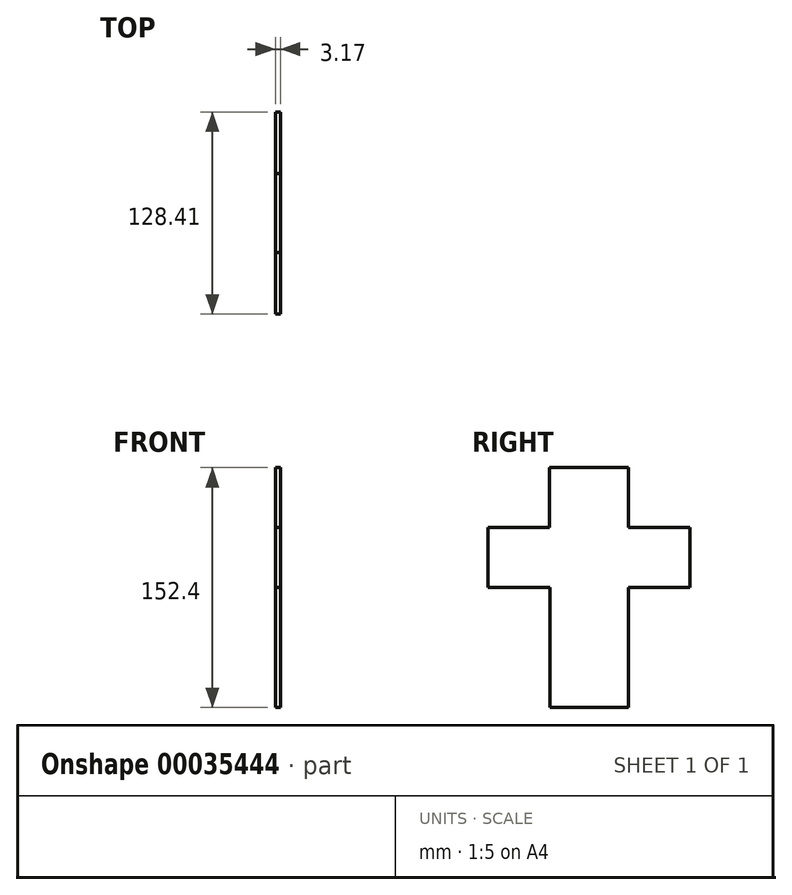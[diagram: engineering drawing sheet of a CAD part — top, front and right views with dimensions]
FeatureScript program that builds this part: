
annotation { "Feature Type Name" : "Feature", "Feature Type Description" : "" }
export const myFeature = defineFeature(function(context is Context, id is Id, definition is map)
    precondition{}
    {
        {
            var Q0;
            Q0=qCreatedBy(makeId("Right.planeOp"),FACE);
            var sketch = newSketch(context, id + "F0", { "sketchPlane" : qUnion([Q0])});
            skLineSegment(sketch, "E0.bottom", {"start": v(0, -2) * mm, "end": v(-49.92, -2) * mm});
            skLineSegment(sketch, "E0.top", {"start": v(0, -40.1) * mm, "end": v(-49.92, -40.1) * mm});
            skLineSegment(sketch, "E0.left", {"start": v(0, -2) * mm, "end": v(0, -40.1) * mm});
            skLineSegment(sketch, "E0.right", {"start": v(-49.92, -2) * mm, "end": v(-49.92, -40.1) * mm});
            skLineSegment(sketch, "E1.bottom", {"start": v(0, -2) * mm, "end": v(-50.15, -2) * mm});
            skLineSegment(sketch, "E1.top", {"start": v(0, 36.1) * mm, "end": v(-50.15, 36.1) * mm});
            skLineSegment(sketch, "E1.left", {"start": v(0, -2) * mm, "end": v(0, 36.1) * mm});
            skLineSegment(sketch, "E1.right", {"start": v(-50.15, -2) * mm, "end": v(-50.15, 36.1) * mm});
            skLineSegment(sketch, "E2.top", {"start": v(0, 74.2) * mm, "end": v(-50.15, 74.2) * mm});
            skLineSegment(sketch, "E2.left", {"start": v(0, 36.1) * mm, "end": v(0, 74.2) * mm});
            skLineSegment(sketch, "E2.right", {"start": v(-50.15, 36.1) * mm, "end": v(-50.15, 74.2) * mm});
            skLineSegment(sketch, "E3.top", {"start": v(0, -78.2) * mm, "end": v(-49.92, -78.2) * mm});
            skLineSegment(sketch, "E3.left", {"start": v(0, -40.1) * mm, "end": v(0, -78.2) * mm});
            skLineSegment(sketch, "E3.right", {"start": v(-49.92, -40.1) * mm, "end": v(-49.92, -78.2) * mm});
            skLineSegment(sketch, "E4.bottom", {"start": v(0, 36.1) * mm, "end": v(39.22, 36.1) * mm});
            skLineSegment(sketch, "E4.top", {"start": v(0, -2) * mm, "end": v(39.22, -2) * mm});
            skLineSegment(sketch, "E4.left", {"start": v(0, 36.1) * mm, "end": v(0, -2) * mm});
            skLineSegment(sketch, "E4.right", {"start": v(39.22, 36.1) * mm, "end": v(39.22, -2) * mm});
            skLineSegment(sketch, "E5.bottom", {"start": v(-50.15, 36.1) * mm, "end": v(-89.2, 36.1) * mm});
            skLineSegment(sketch, "E5.top", {"start": v(-50.15, -2) * mm, "end": v(-89.2, -2) * mm});
            skLineSegment(sketch, "E5.left", {"start": v(-50.15, 36.1) * mm, "end": v(-50.15, -2) * mm});
            skLineSegment(sketch, "E5.right", {"start": v(-89.2, 36.1) * mm, "end": v(-89.2, -2) * mm});
            skSolve(sketch);
        }
        {
            var Q0;
            Q0 = qSketchRegion(id + "F0", true);
            extrude(context, id + "F1", {"entities" : qUnion([Q0]), "depth" : 3.17 * mm});
        }
    });
